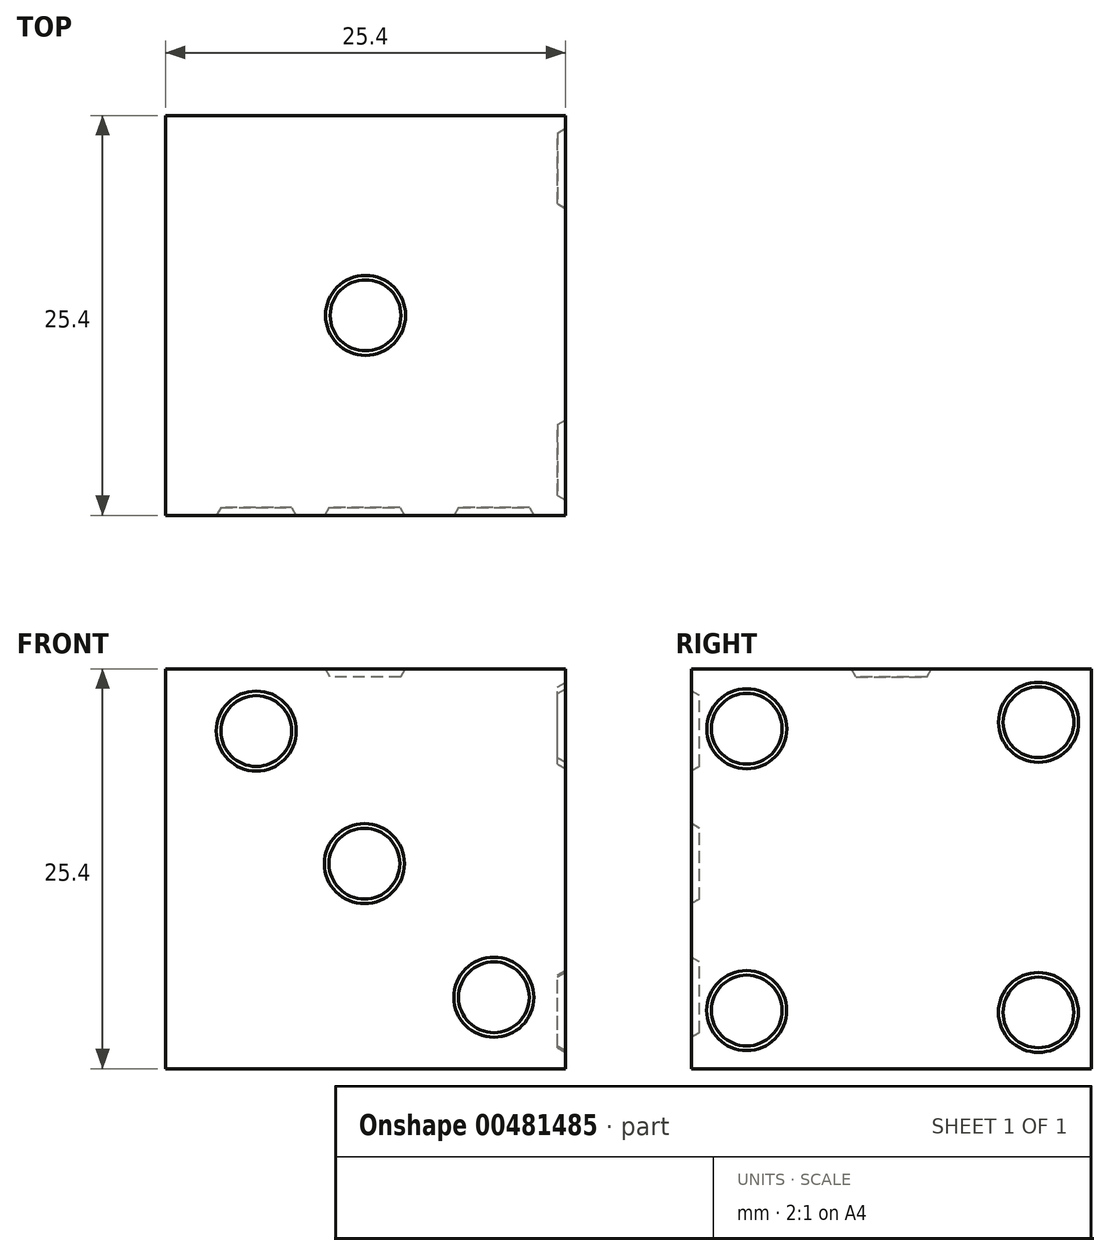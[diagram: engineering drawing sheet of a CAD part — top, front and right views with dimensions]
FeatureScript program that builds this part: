
annotation { "Feature Type Name" : "Feature", "Feature Type Description" : "" }
export const myFeature = defineFeature(function(context is Context, id is Id, definition is map)
    precondition{}
    {
        {
            var Q0;
            Q0=qCreatedBy(makeId("Top.planeOp"),FACE);
            var sketch = newSketch(context, id + "F0", { "sketchPlane" : qUnion([Q0])});
            skLineSegment(sketch, "E0.bottom", {"start": v(-12.7, 12.7) * mm, "end": v(12.7, 12.7) * mm});
            skLineSegment(sketch, "E0.top", {"start": v(-12.7, -12.7) * mm, "end": v(12.7, -12.7) * mm});
            skLineSegment(sketch, "E0.left", {"start": v(-12.7, 12.7) * mm, "end": v(-12.7, -12.7) * mm});
            skLineSegment(sketch, "E0.right", {"start": v(12.7, 12.7) * mm, "end": v(12.7, -12.7) * mm});
            skPoint(sketch, "E0.middle", {"position": v(0, 0) * mm});
            skSolve(sketch);
        }
        {
            var Q0;
            Q0=makeQuery(id+"F0.imprint","IMPRINT",FACE,{"disambiguationData":[TD([[makeQuery(id+"F0.imprint","IMPRINT",EDGE,{"derivedFrom":sQuery(id+"F0.wireOp",EDGE,"E0.bottom")}),-1.0]])]});
            extrude(context, id + "F1", {"entities" : qUnion([Q0]), "depth" : 25.4 * mm});
        }
        {
            var Q0;
            Q0=makeQuery(id+"F1.opExtrude","CAP_FACE",FACE,{"disambiguationData":[OSD([sQuery(id+"F0.wireOp",EDGE,"E0.bottom"),sQuery(id+"F0.wireOp",EDGE,"E0.top"),sQuery(id+"F0.wireOp",EDGE,"E0.left"),sQuery(id+"F0.wireOp",EDGE,"E0.right")])],"isStart":false});
            var sketch = newSketch(context, id + "F2", { "sketchPlane" : qUnion([Q0])});
            skCircle(sketch, "E1", {"center": v(0, 0) * mm, "radius": 2.54 * mm});
            skSolve(sketch);
        }
        {
            var Q0;
            Q0=makeQuery(id+"F2.imprint","IMPRINT",FACE,{"disambiguationData":[TD([[makeQuery(id+"F2.imprint","IMPRINT",EDGE,{"derivedFrom":sQuery(id+"F2.wireOp",EDGE,"E1")}),1.0]])]});
            extrude(context, id + "F3", {"entities" : qUnion([Q0]), "operationType" : NewBodyOperationType.REMOVE, "oppositeDirection" : true, "depth" : 0.5 * mm, "hasDraft" : true, "draftAngle" : 30 * degree, "draftPullDirection" : true});
        }
        {
            var Q0;
            Q0=makeQuery(id+"F1.opExtrude","SWEPT_FACE",FACE,{"disambiguationData":[OSD([sQuery(id+"F0.wireOp",EDGE,"E0.top")])]});
            var sketch = newSketch(context, id + "F4", { "sketchPlane" : qUnion([Q0])});
            skCircle(sketch, "E2", {"center": v(-6.94, 21.45) * mm, "radius": 2.54 * mm});
            skCircle(sketch, "E3", {"center": v(-0.07, 13.02) * mm, "radius": 2.54 * mm});
            skCircle(sketch, "E4", {"center": v(8.15, 4.53) * mm, "radius": 2.54 * mm});
            skSolve(sketch);
        }
        {
            var Q0;
            Q0=makeQuery(id+"F4.imprint","IMPRINT",FACE,{"disambiguationData":[TD([[makeQuery(id+"F4.imprint","IMPRINT",EDGE,{"derivedFrom":sQuery(id+"F4.wireOp",EDGE,"E2")}),1.0]])]});
            var Q1;
            Q1=makeQuery(id+"F4.imprint","IMPRINT",FACE,{"disambiguationData":[TD([[makeQuery(id+"F4.imprint","IMPRINT",EDGE,{"derivedFrom":sQuery(id+"F4.wireOp",EDGE,"E3")}),1.0]])]});
            var Q2;
            Q2=makeQuery(id+"F4.imprint","IMPRINT",FACE,{"disambiguationData":[TD([[makeQuery(id+"F4.imprint","IMPRINT",EDGE,{"derivedFrom":sQuery(id+"F4.wireOp",EDGE,"E4")}),1.0]])]});
            extrude(context, id + "F5", {"entities" : qUnion([Q0, Q1, Q2]), "operationType" : NewBodyOperationType.REMOVE, "oppositeDirection" : true, "depth" : 0.5 * mm, "hasDraft" : true, "draftAngle" : 30 * degree, "draftPullDirection" : true});
        }
        {
            var Q0;
            Q0=makeQuery(id+"F1.opExtrude","SWEPT_FACE",FACE,{"disambiguationData":[OSD([sQuery(id+"F0.wireOp",EDGE,"E0.right")])]});
            var sketch = newSketch(context, id + "F6", { "sketchPlane" : qUnion([Q0])});
            skCircle(sketch, "E5", {"center": v(-9.2, 3.7) * mm, "radius": 2.54 * mm});
            skCircle(sketch, "E6", {"center": v(9.34, 22) * mm, "radius": 2.54 * mm});
            skCircle(sketch, "E7", {"center": v(-9.19, 21.59) * mm, "radius": 2.54 * mm});
            skCircle(sketch, "E8", {"center": v(9.33, 3.57) * mm, "radius": 2.54 * mm});
            skSolve(sketch);
        }
        {
            var Q0;
            Q0=makeQuery(id+"F6.imprint","IMPRINT",FACE,{"disambiguationData":[TD([[makeQuery(id+"F6.imprint","IMPRINT",EDGE,{"derivedFrom":sQuery(id+"F6.wireOp",EDGE,"E7")}),1.0]])]});
            var Q1;
            Q1=makeQuery(id+"F6.imprint","IMPRINT",FACE,{"disambiguationData":[TD([[makeQuery(id+"F6.imprint","IMPRINT",EDGE,{"derivedFrom":sQuery(id+"F6.wireOp",EDGE,"E6")}),1.0]])]});
            var Q2;
            Q2=makeQuery(id+"F6.imprint","IMPRINT",FACE,{"disambiguationData":[TD([[makeQuery(id+"F6.imprint","IMPRINT",EDGE,{"derivedFrom":sQuery(id+"F6.wireOp",EDGE,"E8")}),1.0]])]});
            var Q3;
            Q3=makeQuery(id+"F6.imprint","IMPRINT",FACE,{"disambiguationData":[TD([[makeQuery(id+"F6.imprint","IMPRINT",EDGE,{"derivedFrom":sQuery(id+"F6.wireOp",EDGE,"E5")}),1.0]])]});
            extrude(context, id + "F7", {"entities" : qUnion([Q0, Q1, Q2, Q3]), "operationType" : NewBodyOperationType.REMOVE, "oppositeDirection" : true, "depth" : 0.5 * mm, "hasDraft" : true, "draftAngle" : 30 * degree, "draftPullDirection" : true});
        }
    });
